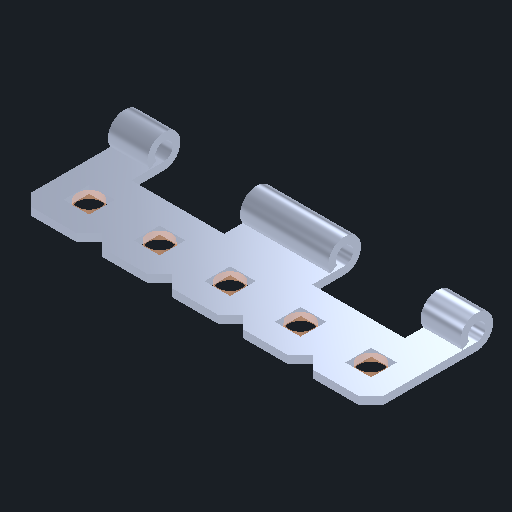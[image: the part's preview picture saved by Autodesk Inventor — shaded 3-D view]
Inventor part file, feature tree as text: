
AUTODESK INVENTOR PART (.ipt)
format: ipt  version: 2024 (Build 280153000, 153)  size: 214,016 bytes
history: native  units: in
note: dims shown in document units (in); Inventor stores cm internally (conversion verified against a paired STEP export)
features: other x7, extrude x5, pattern_linear x1, imported_body x1
ambient origin geometry x8: Origin, YZ Plane, XZ Plane, XY Plane, X Axis, Y Axis, Z Axis, Center Point
bodies: Body1 (feature_tree), Body2 (feature_tree), Body3 (feature_tree), Body4 (feature_tree), Body5 (feature_tree), Body6 (feature_tree)
feature tree (14):
  other  "Cut-Extrude3"
  other  "Top"
  pattern_linear  "Rectangular Pattern1"  Spacing1=0.046in  [1 undecoded]
  imported_body  "Base1"
  other  "Srf1"
  other  "Srf2"
  other  "Srf3"
  other  "Srf4"
  other  "Srf5"
  extrude  "ExtrusionSrf1"  Depth=0.5in
  extrude  "ExtrusionSrf2"  Depth=0.172in
  extrude  "ExtrusionSrf3"  [1 undecoded]
  extrude  "ExtrusionSrf4"  [1 undecoded]
  extrude  "ExtrusionSrf5"  [1 undecoded]
note: 4 required parameter values undecoded (feature->parameter linkage not recoverable at this tier; creation-order binding heuristic only, values carry confidence <= 0.55)
